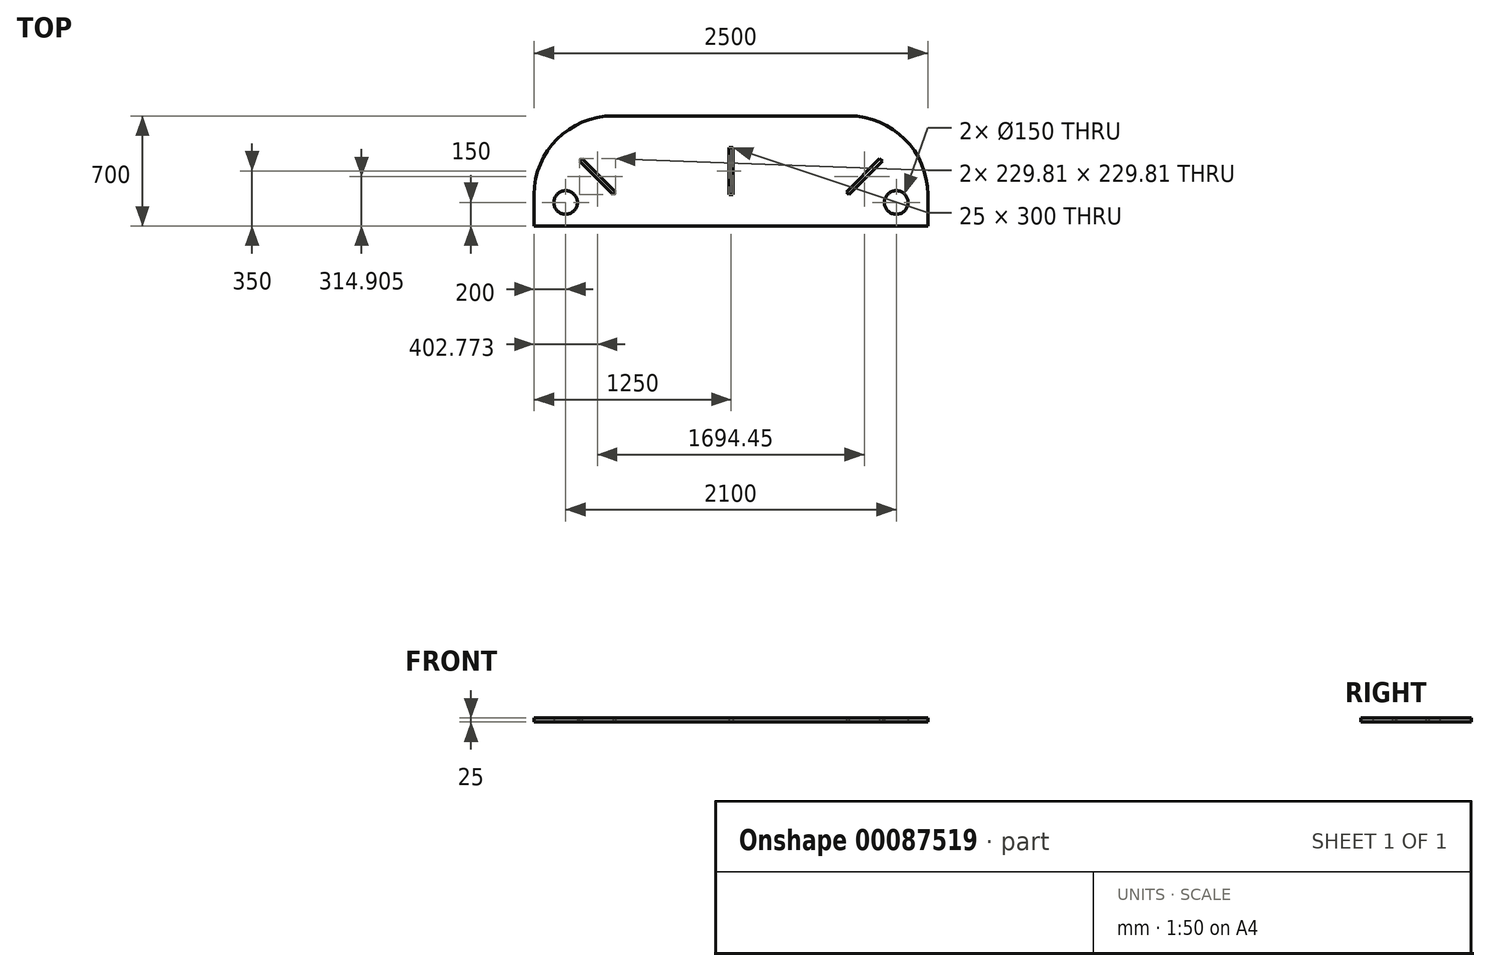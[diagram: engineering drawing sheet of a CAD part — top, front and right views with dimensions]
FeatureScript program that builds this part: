
annotation { "Feature Type Name" : "Feature", "Feature Type Description" : "" }
export const myFeature = defineFeature(function(context is Context, id is Id, definition is map)
    precondition{}
    {
        {
            var Q0;
            Q0=qCreatedBy(makeId("Top.planeOp"),FACE);
            var sketch = newSketch(context, id + "F0", { "sketchPlane" : qUnion([Q0])});
            skLineSegment(sketch, "E0", {"start": v(-500, 0) * mm, "end": v(2000, 0) * mm});
            skLineSegment(sketch, "E1", {"start": v(-500, 0) * mm, "end": v(-500, 200) * mm});
            skLineSegment(sketch, "E2", {"start": v(2000, 0) * mm, "end": v(2000, 200) * mm});
            skArc(sketch, "E3", {"start": v(0, 700) * mm, "mid": v(-353.55, 553.55) * mm, "end": v(-500, 200) * mm});
            skArc(sketch, "E4", {"start": v(2000, 200) * mm, "mid": v(1853.55, 553.55) * mm, "end": v(1500, 700) * mm});
            skLineSegment(sketch, "E5", {"start": v(0, 700) * mm, "end": v(1500, 700) * mm});
            skCircle(sketch, "E6", {"center": v(1800, 150) * mm, "radius": 75 * mm});
            skCircle(sketch, "E7", {"center": v(-300, 150) * mm, "radius": 75 * mm});
            skLineSegment(sketch, "E8", {"start": v(0, 200) * mm, "end": v(-212.13, 412.13) * mm});
            skLineSegment(sketch, "E9", {"start": v(-212.13, 412.13) * mm, "end": v(-194.45, 429.8) * mm});
            skLineSegment(sketch, "E10", {"start": v(-194.45, 429.8) * mm, "end": v(17.68, 217.68) * mm});
            skLineSegment(sketch, "E11", {"start": v(17.68, 217.68) * mm, "end": v(0, 200) * mm});
            skLineSegment(sketch, "E12", {"start": v(1500, 200) * mm, "end": v(1712.13, 412.13) * mm});
            skLineSegment(sketch, "E13", {"start": v(1712.13, 412.13) * mm, "end": v(1694.45, 429.8) * mm});
            skLineSegment(sketch, "E14", {"start": v(1694.45, 429.8) * mm, "end": v(1482.32, 217.68) * mm});
            skLineSegment(sketch, "E15", {"start": v(1482.32, 217.68) * mm, "end": v(1500, 200) * mm});
            skLineSegment(sketch, "E16.bottom", {"start": v(737.5, 500) * mm, "end": v(762.5, 500) * mm});
            skLineSegment(sketch, "E16.top", {"start": v(737.5, 200) * mm, "end": v(762.5, 200) * mm});
            skLineSegment(sketch, "E16.left", {"start": v(737.5, 500) * mm, "end": v(737.5, 200) * mm});
            skLineSegment(sketch, "E16.right", {"start": v(762.5, 500) * mm, "end": v(762.5, 200) * mm});
            skSolve(sketch);
        }
        {
            var Q0;
            Q0=makeQuery(id+"F0.imprint","IMPRINT",FACE,{"disambiguationData":[TD([[makeQuery(id+"F0.imprint","IMPRINT",EDGE,{"derivedFrom":sQuery(id+"F0.wireOp",EDGE,"E0")}),1.0]])]});
            extrude(context, id + "F1", {"entities" : qUnion([Q0]), "depth" : 25 * mm});
        }
    });
